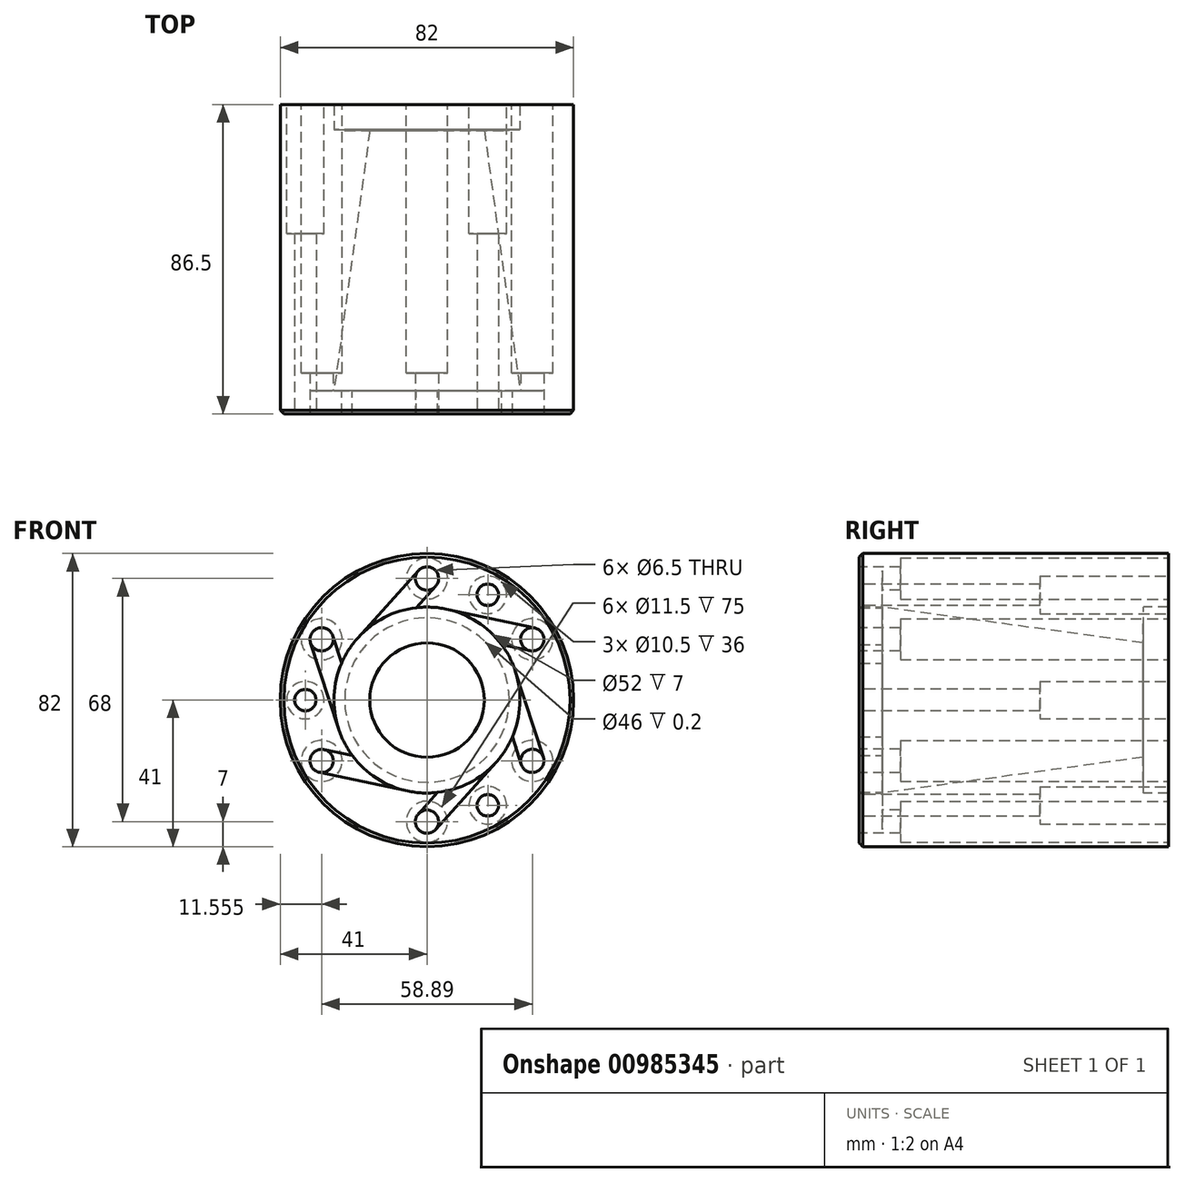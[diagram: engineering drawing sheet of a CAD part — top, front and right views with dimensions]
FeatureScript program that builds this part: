
annotation { "Feature Type Name" : "Feature", "Feature Type Description" : "" }
export const myFeature = defineFeature(function(context is Context, id is Id, definition is map)
    precondition{}
    {
        {
            var Q0;
            Q0=qCreatedBy(makeId("Front.planeOp"),FACE);
            var sketch = newSketch(context, id + "F0", { "sketchPlane" : qUnion([Q0])});
            skCircle(sketch, "E0", {"center": v(0, 0) * mm, "radius": 41 * mm});
            skCircle(sketch, "E1", {"center": v(0, 34) * mm, "radius": 3.25 * mm});
            skCircle(sketch, "E2.1.0", {"center": v(-29.44, 17) * mm, "radius": 3.25 * mm});
            skCircle(sketch, "E2.2.0", {"center": v(-29.44, -17) * mm, "radius": 3.25 * mm});
            skCircle(sketch, "E2.3.0", {"center": v(0, -34) * mm, "radius": 3.25 * mm});
            skCircle(sketch, "E2.4.0", {"center": v(29.44, -17) * mm, "radius": 3.25 * mm});
            skCircle(sketch, "E2.5.0", {"center": v(29.44, 17) * mm, "radius": 3.25 * mm});
            skCircle(sketch, "E3", {"center": v(-34, 0) * mm, "radius": 3 * mm});
            skCircle(sketch, "E4.1.0", {"center": v(17, -29.44) * mm, "radius": 3 * mm});
            skCircle(sketch, "E4.2.0", {"center": v(17, 29.44) * mm, "radius": 3 * mm});
            skSolve(sketch);
        }
        {
            var Q0;
            Q0=qSketchRegion(id+"F0",true);
            extrude(context, id + "F1", {"entities" : qUnion([Q0]), "oppositeDirection" : true, "depth" : 80 * mm});
        }
        {
            var Q0;
            Q0=makeQuery(id+"F1.opExtrude","CAP_FACE",FACE,{"disambiguationData":[OSD([sQuery(id+"F0.wireOp",EDGE,"E0"),sQuery(id+"F0.wireOp",EDGE,"E1"),sQuery(id+"F0.wireOp",EDGE,"E2.1.0"),sQuery(id+"F0.wireOp",EDGE,"E2.2.0"),sQuery(id+"F0.wireOp",EDGE,"E2.3.0"),sQuery(id+"F0.wireOp",EDGE,"E2.4.0"),sQuery(id+"F0.wireOp",EDGE,"E2.5.0"),sQuery(id+"F0.wireOp",EDGE,"E3"),sQuery(id+"F0.wireOp",EDGE,"E4.1.0"),sQuery(id+"F0.wireOp",EDGE,"E4.2.0")])],"isStart":true});
            var sketch = newSketch(context, id + "F2", { "sketchPlane" : qUnion([Q0])});
            skArc(sketch, "E5", {"start": v(-19.32, 17.4) * mm, "mid": v(-21.88, 14.05) * mm, "end": v(-23.86, 10.33) * mm});
            skArc(sketch, "E6.0", {"start": v(2.42, 31.83) * mm, "mid": v(2.17, 36.42) * mm, "end": v(-2.42, 36.17) * mm});
            skCircle(sketch, "E6.1", {"center": v(0, 0) * mm, "radius": 41 * mm});
            skLineSegment(sketch, "E7", {"start": v(-19.32, 17.4) * mm, "end": v(-2.42, 36.17) * mm});
            skLineSegment(sketch, "E8", {"start": v(-2.98, 25.83) * mm, "end": v(2.42, 31.83) * mm});
            skArc(sketch, "E9.1.0", {"start": v(-26.35, 18) * mm, "mid": v(-30.45, 20.1) * mm, "end": v(-32.54, 16) * mm});
            skLineSegment(sketch, "E9.1.1", {"start": v(-24.73, -8.03) * mm, "end": v(-32.54, 16) * mm});
            skLineSegment(sketch, "E9.1.2", {"start": v(-23.86, 10.33) * mm, "end": v(-26.35, 18) * mm});
            skArc(sketch, "E9.2.0", {"start": v(-28.77, -13.82) * mm, "mid": v(-32.62, -16.32) * mm, "end": v(-30.12, -20.18) * mm});
            skLineSegment(sketch, "E9.2.1", {"start": v(-5.4, -25.43) * mm, "end": v(-30.12, -20.18) * mm});
            skLineSegment(sketch, "E9.2.2", {"start": v(-20.88, -15.5) * mm, "end": v(-28.77, -13.82) * mm});
            skArc(sketch, "E9.3.0", {"start": v(-2.42, -31.83) * mm, "mid": v(-2.17, -36.42) * mm, "end": v(2.42, -36.17) * mm});
            skLineSegment(sketch, "E9.3.1", {"start": v(19.32, -17.4) * mm, "end": v(2.42, -36.17) * mm});
            skLineSegment(sketch, "E9.3.2", {"start": v(2.98, -25.83) * mm, "end": v(-2.42, -31.83) * mm});
            skArc(sketch, "E9.4.0", {"start": v(26.35, -18) * mm, "mid": v(30.45, -20.1) * mm, "end": v(32.54, -16) * mm});
            skLineSegment(sketch, "E9.4.1", {"start": v(24.73, 8.03) * mm, "end": v(32.54, -16) * mm});
            skLineSegment(sketch, "E9.4.2", {"start": v(23.86, -10.33) * mm, "end": v(26.35, -18) * mm});
            skArc(sketch, "E9.5.0", {"start": v(28.77, 13.82) * mm, "mid": v(32.62, 16.32) * mm, "end": v(30.12, 20.18) * mm});
            skLineSegment(sketch, "E9.5.1", {"start": v(5.4, 25.43) * mm, "end": v(30.12, 20.18) * mm});
            skLineSegment(sketch, "E9.5.2", {"start": v(20.88, 15.5) * mm, "end": v(28.77, 13.82) * mm});
            skArc(sketch, "E10.trimOffspring", {"start": v(-24.73, -8.03) * mm, "mid": v(-23.1, -11.92) * mm, "end": v(-20.88, -15.5) * mm});
            skArc(sketch, "E11.trimOffspring", {"start": v(-5.4, -25.43) * mm, "mid": v(-1.23, -25.97) * mm, "end": v(2.98, -25.83) * mm});
            skArc(sketch, "E12.trimOffspring", {"start": v(19.32, -17.4) * mm, "mid": v(21.88, -14.05) * mm, "end": v(23.86, -10.33) * mm});
            skArc(sketch, "E13.trimOffspring", {"start": v(24.73, 8.03) * mm, "mid": v(23.1, 11.92) * mm, "end": v(20.88, 15.5) * mm});
            skArc(sketch, "E14.trimOffspring", {"start": v(5.4, 25.43) * mm, "mid": v(1.23, 25.97) * mm, "end": v(-2.98, 25.83) * mm});
            skCircle(sketch, "E15.0", {"center": v(-34, 0) * mm, "radius": 3 * mm});
            skCircle(sketch, "E15.1", {"center": v(17, 29.44) * mm, "radius": 3 * mm});
            skCircle(sketch, "E15.2", {"center": v(17, -29.44) * mm, "radius": 3 * mm});
            skSolve(sketch);
        }
        {
            var Q0;
            Q0=makeQuery(id+"F2.imprint","IMPRINT",FACE,{"disambiguationData":[TD([[makeQuery(id+"F2.imprint","IMPRINT",EDGE,{"derivedFrom":sQuery(id+"F2.wireOp",EDGE,"E5")}),-1.0]])]});
            extrude(context, id + "F3", {"entities" : qUnion([Q0]), "operationType" : NewBodyOperationType.ADD, "depth" : 6.5 * mm});
        }
        {
            var Q0;
            Q0=qCreatedBy(makeId("Top.planeOp"),FACE);
            var sketch = newSketch(context, id + "F4", { "sketchPlane" : qUnion([Q0])});
            skLineSegment(sketch, "E16", {"start": v(0, 80) * mm, "end": v(0, -6.5) * mm});
            skLineSegment(sketch, "E17", {"start": v(0, -6.5) * mm, "end": v(26, -6.5) * mm});
            skLineSegment(sketch, "E18", {"start": v(23, 73) * mm, "end": v(26, 73) * mm});
            skLineSegment(sketch, "E19", {"start": v(26, 73) * mm, "end": v(26, 80) * mm});
            skLineSegment(sketch, "E20", {"start": v(26, 80) * mm, "end": v(0, 80) * mm});
            skLineSegment(sketch, "E21", {"start": v(26, 0) * mm, "end": v(26, -6.5) * mm});
            skLineSegment(sketch, "E22", {"start": v(23, 73) * mm, "end": v(23, 72.8) * mm});
            skLineSegment(sketch, "E23", {"start": v(23, 72.8) * mm, "end": v(16, 72.8) * mm});
            skLineSegment(sketch, "E24", {"start": v(16, 72.8) * mm, "end": v(26, 0) * mm});
            skSolve(sketch);
        }
        {
            var Q0;
            Q0=qSketchRegion(id+"F4",true);
            var Q1;
            Q1=sQuery(id+"F4.wireOp",EDGE,"E16");
            revolve(context, id + "F5", {"operationType" : NewBodyOperationType.REMOVE, "entities" : qUnion([Q0]), "axis" : qUnion([Q1]), "revolveType" : RevolveType.FULL, "oppositeDirection" : true});
        }
        {
            var Q0;
            Q0=makeQuery(id+"F1.opExtrude","CAP_FACE",FACE,{"disambiguationData":[OSD([sQuery(id+"F0.wireOp",EDGE,"E0"),sQuery(id+"F0.wireOp",EDGE,"E1"),sQuery(id+"F0.wireOp",EDGE,"E2.1.0"),sQuery(id+"F0.wireOp",EDGE,"E2.2.0"),sQuery(id+"F0.wireOp",EDGE,"E2.3.0"),sQuery(id+"F0.wireOp",EDGE,"E2.4.0"),sQuery(id+"F0.wireOp",EDGE,"E2.5.0"),sQuery(id+"F0.wireOp",EDGE,"E3"),sQuery(id+"F0.wireOp",EDGE,"E4.1.0"),sQuery(id+"F0.wireOp",EDGE,"E4.2.0")])],"isStart":false});
            var sketch = newSketch(context, id + "F6", { "sketchPlane" : qUnion([Q0])});
            skCircle(sketch, "E25", {"center": v(0, 34) * mm, "radius": 5.75 * mm});
            skCircle(sketch, "E26.1.0", {"center": v(-29.44, 17) * mm, "radius": 5.75 * mm});
            skCircle(sketch, "E26.2.0", {"center": v(-29.44, -17) * mm, "radius": 5.75 * mm});
            skCircle(sketch, "E26.3.0", {"center": v(0, -34) * mm, "radius": 5.75 * mm});
            skCircle(sketch, "E26.4.0", {"center": v(29.44, -17) * mm, "radius": 5.75 * mm});
            skCircle(sketch, "E26.5.0", {"center": v(29.44, 17) * mm, "radius": 5.75 * mm});
            skPoint(sketch, "E26.center", {"position": v(0, 0) * mm});
            skCircle(sketch, "E27", {"center": v(-17, 29.44) * mm, "radius": 5.25 * mm});
            skCircle(sketch, "E28.1.0", {"center": v(-17, -29.44) * mm, "radius": 5.25 * mm});
            skCircle(sketch, "E28.2.0", {"center": v(34, 0) * mm, "radius": 5.25 * mm});
            skSolve(sketch);
        }
        {
            var Q0;
            Q0=makeQuery(id+"F6.imprint","IMPRINT",FACE,{"disambiguationData":[TD([[makeQuery(id+"F6.imprint","IMPRINT",EDGE,{"derivedFrom":sQuery(id+"F6.wireOp",EDGE,"E25")}),1.0]])]});
            var Q1;
            Q1=makeQuery(id+"F6.imprint","IMPRINT",FACE,{"disambiguationData":[TD([[makeQuery(id+"F6.imprint","IMPRINT",EDGE,{"derivedFrom":sQuery(id+"F6.wireOp",EDGE,"E26.1.0")}),1.0]])]});
            var Q2;
            Q2=makeQuery(id+"F6.imprint","IMPRINT",FACE,{"disambiguationData":[TD([[makeQuery(id+"F6.imprint","IMPRINT",EDGE,{"derivedFrom":sQuery(id+"F6.wireOp",EDGE,"E26.2.0")}),1.0]])]});
            var Q3;
            Q3=makeQuery(id+"F6.imprint","IMPRINT",FACE,{"disambiguationData":[TD([[makeQuery(id+"F6.imprint","IMPRINT",EDGE,{"derivedFrom":sQuery(id+"F6.wireOp",EDGE,"E26.3.0")}),1.0]])]});
            var Q4;
            Q4=makeQuery(id+"F6.imprint","IMPRINT",FACE,{"disambiguationData":[TD([[makeQuery(id+"F6.imprint","IMPRINT",EDGE,{"derivedFrom":sQuery(id+"F6.wireOp",EDGE,"E26.4.0")}),1.0]])]});
            var Q5;
            Q5=makeQuery(id+"F6.imprint","IMPRINT",FACE,{"disambiguationData":[TD([[makeQuery(id+"F6.imprint","IMPRINT",EDGE,{"derivedFrom":sQuery(id+"F6.wireOp",EDGE,"E26.5.0")}),1.0]])]});
            extrude(context, id + "F7", {"entities" : qUnion([Q0, Q1, Q2, Q3, Q4, Q5]), "operationType" : NewBodyOperationType.REMOVE, "oppositeDirection" : true, "depth" : 75 * mm});
        }
        {
            var Q0;
            Q0=makeQuery(id+"F6.imprint","IMPRINT",FACE,{"disambiguationData":[TD([[makeQuery(id+"F6.imprint","IMPRINT",EDGE,{"derivedFrom":sQuery(id+"F6.wireOp",EDGE,"E28.1.0")}),1.0]])]});
            var Q1;
            Q1=makeQuery(id+"F6.imprint","IMPRINT",FACE,{"disambiguationData":[TD([[makeQuery(id+"F6.imprint","IMPRINT",EDGE,{"derivedFrom":sQuery(id+"F6.wireOp",EDGE,"E28.2.0")}),1.0]])]});
            var Q2;
            Q2=makeQuery(id+"F6.imprint","IMPRINT",FACE,{"disambiguationData":[TD([[makeQuery(id+"F6.imprint","IMPRINT",EDGE,{"derivedFrom":sQuery(id+"F6.wireOp",EDGE,"E27")}),1.0]])]});
            extrude(context, id + "F8", {"entities" : qUnion([Q0, Q1, Q2]), "operationType" : NewBodyOperationType.REMOVE, "oppositeDirection" : true, "depth" : 36 * mm});
        }
        {
            var Q0;
            Q0=makeQuery(id+"F3.opExtrude","CAP_EDGE",EDGE,{"disambiguationData":[OSD([sQuery(id+"F2.wireOp",EDGE,"E6.1")])],"isStart":false});
            chamfer(context, id + "F9", {"entities" : qUnion([Q0]), "width" : 1 * mm, "tangentPropagation" : true});
        }
    });
